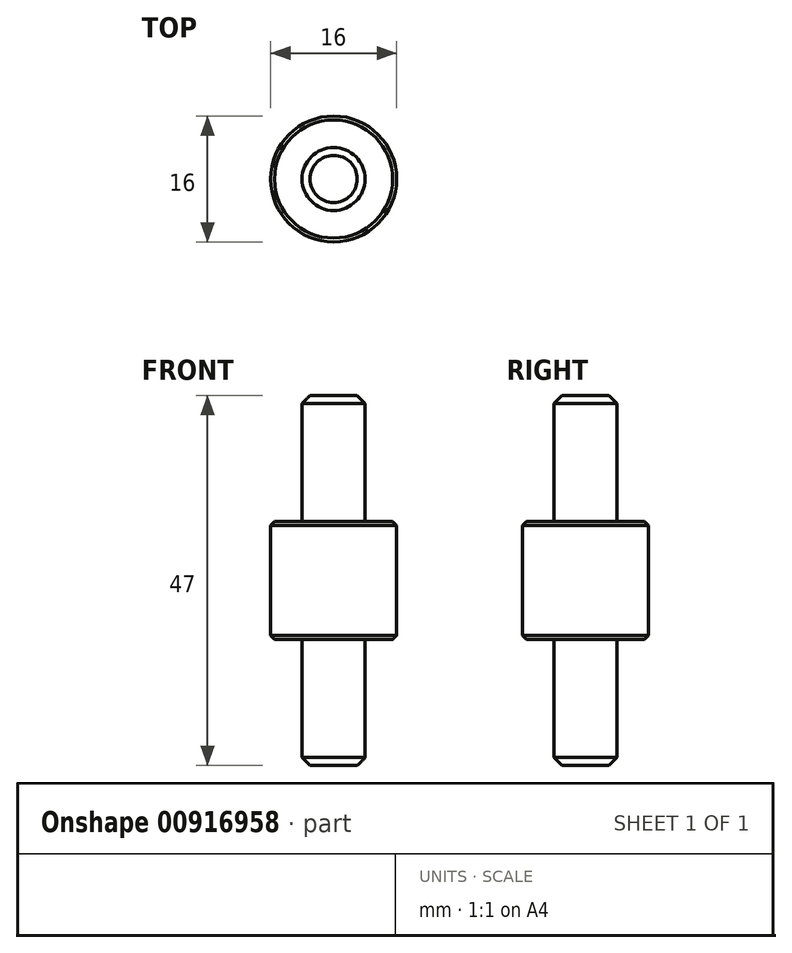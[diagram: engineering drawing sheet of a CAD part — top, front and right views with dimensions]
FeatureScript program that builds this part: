
annotation { "Feature Type Name" : "Feature", "Feature Type Description" : "" }
export const myFeature = defineFeature(function(context is Context, id is Id, definition is map)
    precondition{}
    {
        {
            var Q0;
            Q0=qCreatedBy(makeId("Front.planeOp"),FACE);
            var sketch = newSketch(context, id + "F0", { "sketchPlane" : qUnion([Q0])});
            skLineSegment(sketch, "E0", {"start": v(0, 0) * mm, "end": v(0, 47) * mm});
            skLineSegment(sketch, "E1", {"start": v(0, 47) * mm, "end": v(4, 47) * mm});
            skLineSegment(sketch, "E2", {"start": v(4, 47) * mm, "end": v(4, 31) * mm});
            skLineSegment(sketch, "E3", {"start": v(4, 31) * mm, "end": v(8, 31) * mm});
            skLineSegment(sketch, "E4", {"start": v(8, 31) * mm, "end": v(8, 16) * mm});
            skLineSegment(sketch, "E5", {"start": v(8, 16) * mm, "end": v(4, 16) * mm});
            skLineSegment(sketch, "E6", {"start": v(4, 16) * mm, "end": v(4, 0) * mm});
            skLineSegment(sketch, "E7", {"start": v(4, 0) * mm, "end": v(0, 0) * mm});
            skSolve(sketch);
        }
        {
            var Q0;
            Q0=makeQuery(id+"F0.imprint","IMPRINT",FACE,{"disambiguationData":[TD([[makeQuery(id+"F0.imprint","IMPRINT",EDGE,{"derivedFrom":sQuery(id+"F0.wireOp",EDGE,"E0")}),-1.0]])]});
            var Q1;
            Q1=sQuery(id+"F0.wireOp",EDGE,"E0");
            revolve(context, id + "F1", {"surfaceOperationType" : NewSurfaceOperationType.NEW, "entities" : qUnion([Q0]), "axis" : qUnion([Q1]), "revolveType" : RevolveType.FULL});
        }
        {
            var Q0;
            Q0=makeQuery(id+"F1.opRevolve","SWEPT_EDGE",EDGE,{"disambiguationData":[OSD([sQuery(id+"F0.wireOp",EDGE,"E3"),sQuery(id+"F0.wireOp",EDGE,"E4")])]});
            var Q1;
            Q1=makeQuery(id+"F1.opRevolve","SWEPT_EDGE",EDGE,{"disambiguationData":[OSD([sQuery(id+"F0.wireOp",EDGE,"E4"),sQuery(id+"F0.wireOp",EDGE,"E5")])]});
            chamfer(context, id + "F2", {"entities" : qUnion([Q0, Q1]), "width" : .5 * mm, "tangentPropagation" : true});
        }
        {
            var Q0;
            Q0=makeQuery(id+"F1.opRevolve","SWEPT_EDGE",EDGE,{"disambiguationData":[OSD([sQuery(id+"F0.wireOp",EDGE,"E1"),sQuery(id+"F0.wireOp",EDGE,"E2")])]});
            var Q1;
            Q1=makeQuery(id+"F1.opRevolve","SWEPT_EDGE",EDGE,{"disambiguationData":[OSD([sQuery(id+"F0.wireOp",EDGE,"E6"),sQuery(id+"F0.wireOp",EDGE,"E7")])]});
            chamfer(context, id + "F3", {"entities" : qUnion([Q0, Q1]), "width" : 1 * mm, "tangentPropagation" : true});
        }
    });
